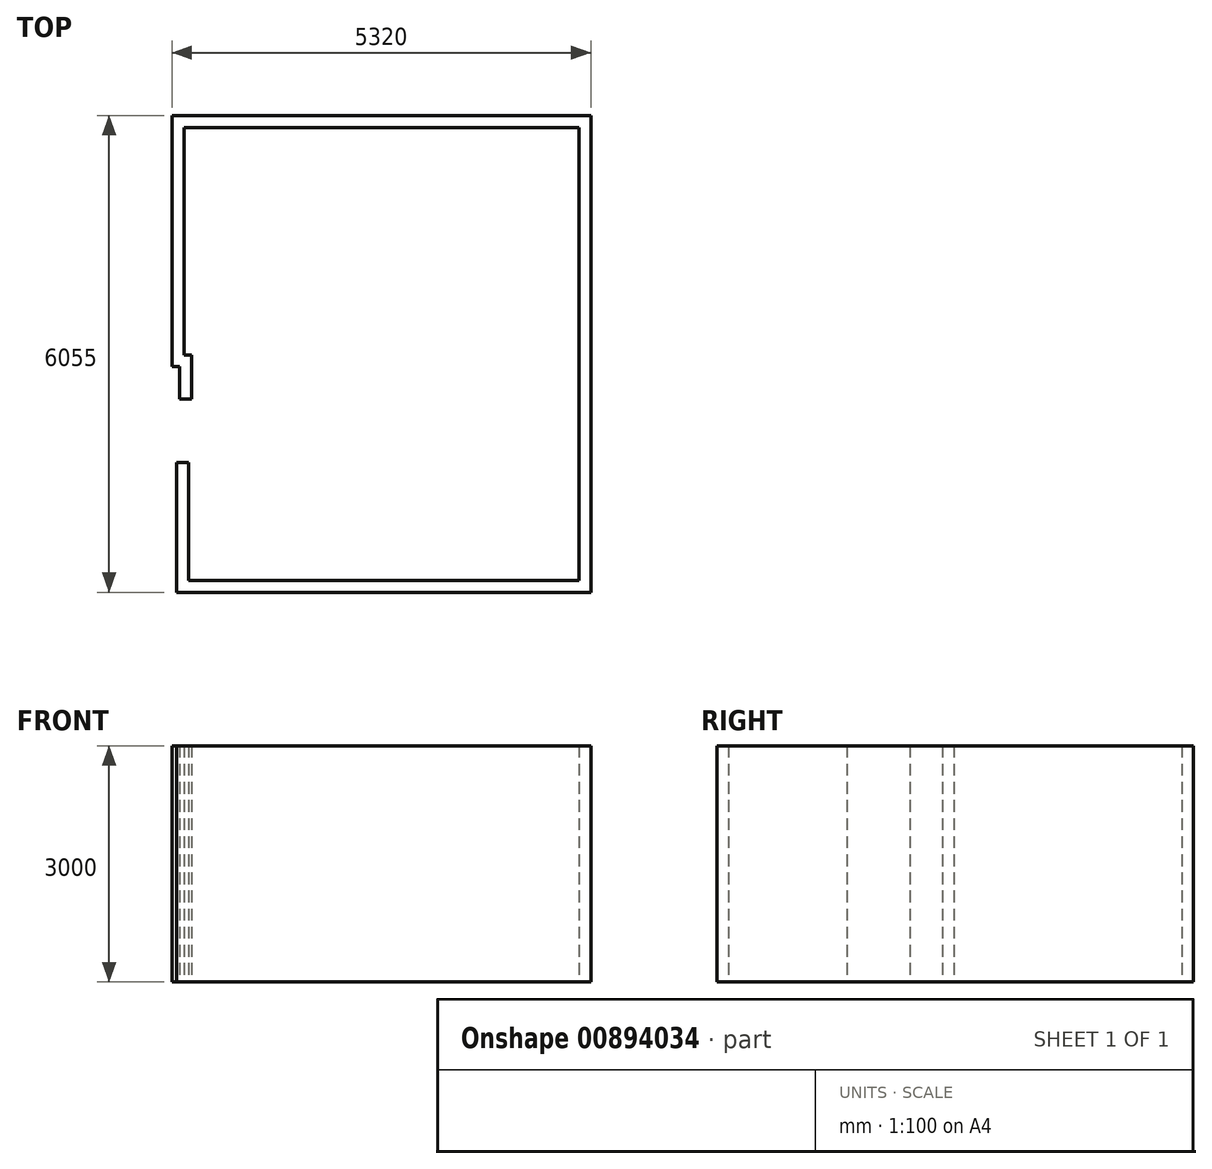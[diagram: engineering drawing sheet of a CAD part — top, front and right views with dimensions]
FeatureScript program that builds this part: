
annotation { "Feature Type Name" : "Feature", "Feature Type Description" : "" }
export const myFeature = defineFeature(function(context is Context, id is Id, definition is map)
    precondition{}
    {
        {
            var Q0;
            Q0=qCreatedBy(makeId("Top.planeOp"),FACE);
            var sketch = newSketch(context, id + "F0", { "sketchPlane" : qUnion([Q0])});
            skLineSegment(sketch, "E0", {"start": v(629.07, 2890) * mm, "end": v(5649.07, 2890) * mm});
            skLineSegment(sketch, "E1", {"start": v(629.07, 2890) * mm, "end": v(629.07, 0) * mm});
            skLineSegment(sketch, "E2", {"start": v(689.07, -1365) * mm, "end": v(689.07, -2865) * mm});
            skLineSegment(sketch, "E3", {"start": v(689.07, -2865) * mm, "end": v(5649.07, -2865) * mm});
            skPoint(sketch, "E4.end.orphan", {"position": v(5984.77, 0) * mm});
            skLineSegment(sketch, "E5", {"start": v(5649.07, -2865) * mm, "end": v(5649.07, 2890) * mm});
            skLineSegment(sketch, "E6", {"start": v(629.07, 0) * mm, "end": v(724.07, 0) * mm});
            skLineSegment(sketch, "E7", {"start": v(724.07, 0) * mm, "end": v(724.07, -560) * mm});
            skLineSegment(sketch, "E8.0", {"start": v(539.07, -1365) * mm, "end": v(539.07, -3015) * mm});
            skLineSegment(sketch, "E8.1", {"start": v(539.07, -3015) * mm, "end": v(5799.07, -3015) * mm});
            skLineSegment(sketch, "E8.2", {"start": v(5799.07, -3015) * mm, "end": v(5799.07, 3040) * mm});
            skLineSegment(sketch, "E8.3", {"start": v(574.07, -150) * mm, "end": v(574.07, -560) * mm});
            skLineSegment(sketch, "E8.4", {"start": v(479.07, -150) * mm, "end": v(574.07, -150) * mm});
            skLineSegment(sketch, "E8.5", {"start": v(479.07, 3040) * mm, "end": v(479.07, -150) * mm});
            skLineSegment(sketch, "E8.6", {"start": v(479.07, 3040) * mm, "end": v(5799.07, 3040) * mm});
            skLineSegment(sketch, "E9", {"start": v(539.07, -1365) * mm, "end": v(689.07, -1365) * mm});
            skLineSegment(sketch, "E10", {"start": v(574.07, -560) * mm, "end": v(724.07, -560) * mm});
            skSolve(sketch);
        }
        {
            var Q0;
            Q0 = qSketchRegion(id + "F0", true);
            extrude(context, id + "F1", {"entities" : qUnion([Q0]), "depth" : 3000 * mm, "offsetDistance" : 25 * mm});
        }
    });
